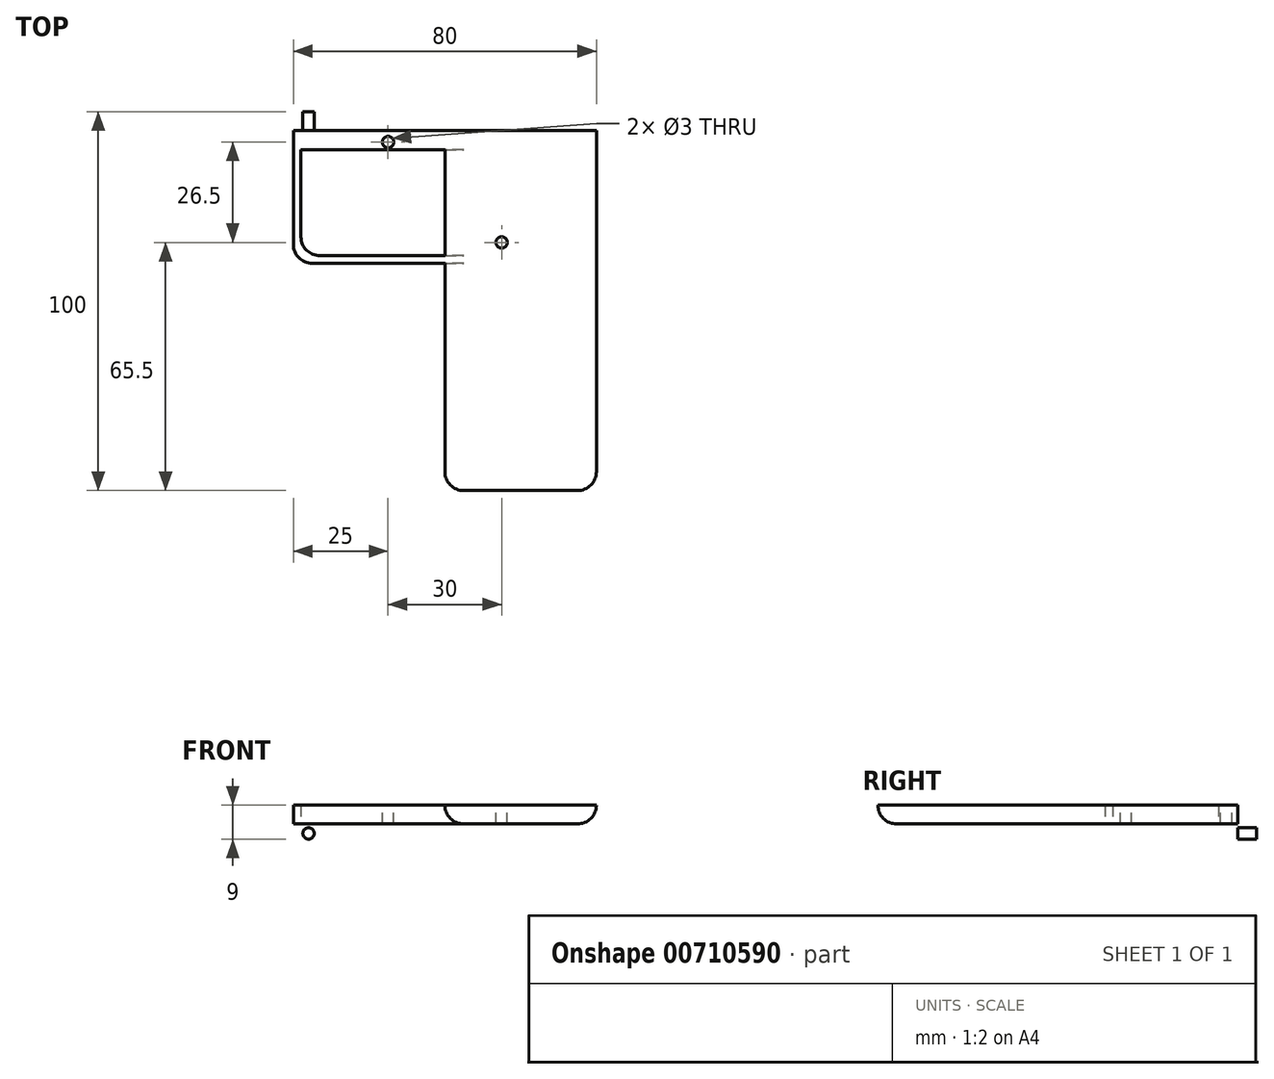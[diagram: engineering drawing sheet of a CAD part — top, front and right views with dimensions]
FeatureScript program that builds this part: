
annotation { "Feature Type Name" : "Feature", "Feature Type Description" : "" }
export const myFeature = defineFeature(function(context is Context, id is Id, definition is map)
    precondition{}
    {
        {
            var Q0;
            Q0=qCreatedBy(makeId("Top.planeOp"),FACE);
            var sketch = newSketch(context, id + "F0", { "sketchPlane" : qUnion([Q0])});
            skLineSegment(sketch, "E0.bottom", {"start": v(20, 50) * mm, "end": v(-20, 50) * mm});
            skLineSegment(sketch, "E0.top", {"start": v(20, -50) * mm, "end": v(-20, -50) * mm});
            skLineSegment(sketch, "E0.left", {"start": v(20, 50) * mm, "end": v(20, -50) * mm});
            skLineSegment(sketch, "E0.right", {"start": v(-20, 50) * mm, "end": v(-20, -50) * mm});
            skPoint(sketch, "E0.middle", {"position": v(0, 0) * mm});
            skLineSegment(sketch, "E1.bottom", {"start": v(-20, 50) * mm, "end": v(-60, 50) * mm});
            skLineSegment(sketch, "E1.top", {"start": v(-20, 10) * mm, "end": v(-60, 10) * mm});
            skLineSegment(sketch, "E1.left", {"start": v(-20, 50) * mm, "end": v(-20, 10) * mm});
            skLineSegment(sketch, "E1.right", {"start": v(-60, 50) * mm, "end": v(-60, 10) * mm});
            skLineSegment(sketch, "E2", {"start": v(-60, 50) * mm, "end": v(-58, 50) * mm});
            skLineSegment(sketch, "E3", {"start": v(-58, 50) * mm, "end": v(-58, 40) * mm});
            skLineSegment(sketch, "E4", {"start": v(-20, 10) * mm, "end": v(-20, 12) * mm});
            skLineSegment(sketch, "E5.bottom", {"start": v(-20, 12) * mm, "end": v(-58, 12) * mm});
            skLineSegment(sketch, "E5.top", {"start": v(-20, 40) * mm, "end": v(-58, 40) * mm});
            skLineSegment(sketch, "E5.left", {"start": v(-20, 12) * mm, "end": v(-20, 40) * mm});
            skLineSegment(sketch, "E5.right", {"start": v(-58, 12) * mm, "end": v(-58, 40) * mm});
            skSolve(sketch);
        }
        {
            var Q0;
            Q0=makeQuery(id+"F0.imprint","IMPRINT",FACE,{"disambiguationData":[TD([[makeQuery(id+"F0.imprint","IMPRINT",EDGE,{"derivedFrom":sQuery(id+"F0.wireOp",EDGE,"E0.bottom")}),1.0]])]});
            var Q1;
            Q1=makeQuery(id+"F0.imprint","IMPRINT",FACE,{"disambiguationData":[TD([[makeQuery(id+"F0.imprint","IMPRINT",EDGE,{"derivedFrom":sQuery(id+"F0.wireOp",EDGE,"E1.bottom")}),1.0]])]});
            var Q2;
            Q2=makeQuery(id+"F0.imprint","IMPRINT",FACE,{"disambiguationData":[TD([[makeQuery(id+"F0.imprint","IMPRINT",EDGE,{"derivedFrom":sQuery(id+"F0.wireOp",EDGE,"E1.top")}),-1.0]])]});
            extrude(context, id + "F1", {"entities" : qUnion([Q0, Q1, Q2]), "depth" : 5 * mm, "offsetDistance" : 25 * mm});
        }
        {
            var Q0;
            Q0=makeQuery(id+"F1.opExtrude","CAP_FACE",FACE,{"disambiguationData":[OSD([sQuery(id+"F0.wireOp",EDGE,"E0.bottom"),sQuery(id+"F0.wireOp",EDGE,"E0.top"),sQuery(id+"F0.wireOp",EDGE,"E0.left"),sQuery(id+"F0.wireOp",EDGE,"E0.right"),sQuery(id+"F0.wireOp",EDGE,"E1.bottom"),sQuery(id+"F0.wireOp",EDGE,"E1.top"),sQuery(id+"F0.wireOp",EDGE,"E1.right"),sQuery(id+"F0.wireOp",EDGE,"E2"),sQuery(id+"F0.wireOp",EDGE,"E5.bottom"),sQuery(id+"F0.wireOp",EDGE,"E5.top"),sQuery(id+"F0.wireOp",EDGE,"E5.left"),sQuery(id+"F0.wireOp",EDGE,"E5.right")])],"isStart":false});
            var sketch = newSketch(context, id + "F2", { "sketchPlane" : qUnion([Q0])});
            skLineSegment(sketch, "E6", {"start": v(-20, 40) * mm, "end": v(-35, 40) * mm, "construction": true});
            skLineSegment(sketch, "E7", {"start": v(-35, 40) * mm, "end": v(-35, 42) * mm, "construction": true});
            skCircle(sketch, "E8", {"center": v(-35, 42) * mm, "radius": 1.5 * mm});
            skLineSegment(sketch, "E9", {"start": v(-35, 42) * mm, "end": v(-35, 18.5) * mm, "construction": true});
            skLineSegment(sketch, "E10", {"start": v(-35, 18.5) * mm, "end": v(-5, 18.5) * mm, "construction": true});
            skLineSegment(sketch, "E11", {"start": v(-5, 18.5) * mm, "end": v(-5, 15.5) * mm, "construction": true});
            skCircle(sketch, "E12", {"center": v(-5, 15.5) * mm, "radius": 1.5 * mm});
            skLineSegment(sketch, "E13", {"start": v(20, 50) * mm, "end": v(20, 45) * mm});
            skLineSegment(sketch, "E14", {"start": v(20, 45) * mm, "end": v(15, 45) * mm});
            skLineSegment(sketch, "E15", {"start": v(15, 45) * mm, "end": v(15, 50) * mm});
            skSolve(sketch);
        }
        {
            var Q0;
            Q0=makeQuery(id+"F2.imprint","IMPRINT",FACE,{"disambiguationData":[TD([[makeQuery(id+"F2.imprint","IMPRINT",EDGE,{"derivedFrom":sQuery(id+"F2.wireOp",EDGE,"E8")}),1.0]])]});
            var Q1;
            Q1=makeQuery(id+"F2.imprint","IMPRINT",FACE,{"disambiguationData":[TD([[makeQuery(id+"F2.imprint","IMPRINT",EDGE,{"derivedFrom":sQuery(id+"F2.wireOp",EDGE,"E12")}),1.0]])]});
            var Q2;
            Q2=makeQuery(id+"F2.imprint","IMPRINT",FACE,{"disambiguationData":[TD([[makeQuery(id+"F2.imprint","IMPRINT",EDGE,{"derivedFrom":sQuery(id+"F2.wireOp",EDGE,"vCmjWVmu-7WJX-9hG4-9sAc-bVtIOR9l7AIR")}),1.0]])]});
            extrude(context, id + "F3", {"entities" : qUnion([Q0, Q1, Q2]), "operationType" : NewBodyOperationType.REMOVE, "oppositeDirection" : true, "depth" : 5 * mm, "offsetDistance" : 25 * mm});
        }
        {
            var Q0;
            Q0=makeQuery(id+"F1.opExtrude","CAP_FACE",FACE,{"disambiguationData":[OSD([sQuery(id+"F0.wireOp",EDGE,"E0.bottom"),sQuery(id+"F0.wireOp",EDGE,"E0.top"),sQuery(id+"F0.wireOp",EDGE,"E0.left"),sQuery(id+"F0.wireOp",EDGE,"E0.right"),sQuery(id+"F0.wireOp",EDGE,"E1.bottom"),sQuery(id+"F0.wireOp",EDGE,"E1.top"),sQuery(id+"F0.wireOp",EDGE,"E1.right"),sQuery(id+"F0.wireOp",EDGE,"E2"),sQuery(id+"F0.wireOp",EDGE,"E5.bottom"),sQuery(id+"F0.wireOp",EDGE,"E5.top"),sQuery(id+"F0.wireOp",EDGE,"E5.left"),sQuery(id+"F0.wireOp",EDGE,"E5.right")])],"isStart":true});
            var sketch = newSketch(context, id + "F4", { "sketchPlane" : qUnion([Q0])});
            skLineSegment(sketch, "E16", {"start": v(20, -50) * mm, "end": v(12, -50) * mm});
            skLineSegment(sketch, "E17", {"start": v(12, -50) * mm, "end": v(12, -45) * mm});
            skLineSegment(sketch, "E18", {"start": v(12, -45) * mm, "end": v(20, -45) * mm});
            skLineSegment(sketch, "E19.MirrorCS", {"start": v(-52, -50) * mm, "end": v(-52, -45) * mm});
            skLineSegment(sketch, "E20.MirrorCS", {"start": v(-52, -45) * mm, "end": v(-60, -45) * mm});
            skSolve(sketch);
        }
        {
            var Q0;
            {var subQ0=sQuery(id+"F4.wireOp",EDGE,"E16");Q0=makeQuery(id+"F4.imprint","IMPRINT",FACE,{"disambiguationData":[TD([[makeQuery(id+"F4.imprint","IMPRINT",EDGE,{"derivedFrom":subQ0}),-1.0]])]});}
            var Q1;
            {var subQ0=sQuery(id+"F4.wireOp",EDGE,"E19.MirrorCS");Q1=makeQuery(id+"F4.imprint","IMPRINT",FACE,{"disambiguationData":[TD([[makeQuery(id+"F4.imprint","IMPRINT",EDGE,{"derivedFrom":subQ0}),1.0]])]});}
            extrude(context, id + "F5", {"entities" : qUnion([Q0, Q1]), "operationType" : NewBodyOperationType.ADD, "depth" : 5 * mm, "offsetDistance" : 25 * mm});
        }
        {
            var Q0;
            Q0=makeQuery(id+"F5.boolean.opBoolean","MERGE",FACE,{"derivedFrom":[makeQuery(id+"F1.opExtrude","SWEPT_FACE",FACE,{"disambiguationData":[OSD([sQuery(id+"F0.wireOp",EDGE,"E0.bottom"),sQuery(id+"F0.wireOp",EDGE,"E1.bottom"),sQuery(id+"F0.wireOp",EDGE,"E2")])]}),makeQuery(id+"F5.opExtrude","SWEPT_FACE",FACE,{"disambiguationData":[OSD([sQuery(id+"F4.wireOp",EDGE,"E16")])]})]});
            var sketch = newSketch(context, id + "F6", { "sketchPlane" : qUnion([Q0])});
            skLineSegment(sketch, "E21", {"start": v(-20, -5) * mm, "end": v(-20, -2.5) * mm});
            skLineSegment(sketch, "E22", {"start": v(-20, -2.5) * mm, "end": v(-16, -2.5) * mm});
            skCircle(sketch, "E23", {"center": v(-16, -2.5) * mm, "radius": 1.5 * mm});
            skLineSegment(sketch, "E24", {"start": v(20, 0) * mm, "end": v(20, 5) * mm, "construction": true});
            skCircle(sketch, "E25.MirrorC", {"center": v(56, -2.5) * mm, "radius": 1.5 * mm});
            skSolve(sketch);
        }
        {
            var Q0;
            Q0=makeQuery(id+"F6.imprint","IMPRINT",FACE,{"disambiguationData":[TD([[makeQuery(id+"F6.imprint","IMPRINT",EDGE,{"derivedFrom":sQuery(id+"F6.wireOp",EDGE,"E23")}),1.0]])]});
            var Q1;
            Q1=makeQuery(id+"F6.imprint","IMPRINT",FACE,{"disambiguationData":[TD([[makeQuery(id+"F6.imprint","IMPRINT",EDGE,{"derivedFrom":sQuery(id+"F6.wireOp",EDGE,"E25.MirrorC")}),-1.0]])]});
            extrude(context, id + "F7", {"entities" : qUnion([Q0, Q1]), "operationType" : NewBodyOperationType.REMOVE, "oppositeDirection" : true, "depth" : 5 * mm, "offsetDistance" : 25 * mm});
        }
        {
            var Q0;
            Q0=makeQuery(id+"F1.opExtrude","CAP_EDGE",EDGE,{"disambiguationData":[OSD([sQuery(id+"F0.wireOp",EDGE,"E0.left")])],"isStart":true});
            var Q1;
            Q1=makeQuery(id+"F1.opExtrude","CAP_EDGE",EDGE,{"disambiguationData":[OSD([sQuery(id+"F0.wireOp",EDGE,"E5.left")])],"isStart":true});
            var Q2;
            Q2=makeQuery(id+"F1.opExtrude","CAP_EDGE",EDGE,{"disambiguationData":[OSD([sQuery(id+"F0.wireOp",EDGE,"E0.right")])],"isStart":true});
            var Q3;
            Q3=makeQuery(id+"F1.opExtrude","SWEPT_EDGE",EDGE,{"disambiguationData":[OSD([sQuery(id+"F0.wireOp",EDGE,"E0.top"),sQuery(id+"F0.wireOp",EDGE,"E0.left")])]});
            var Q4;
            Q4=makeQuery(id+"F1.opExtrude","CAP_EDGE",EDGE,{"disambiguationData":[OSD([sQuery(id+"F0.wireOp",EDGE,"E0.top")])],"isStart":true});
            var Q5;
            Q5=makeQuery(id+"F1.opExtrude","SWEPT_EDGE",EDGE,{"disambiguationData":[OSD([sQuery(id+"F0.wireOp",EDGE,"E0.top"),sQuery(id+"F0.wireOp",EDGE,"E0.right")])]});
            var Q6;
            Q6=makeQuery(id+"F1.opExtrude","SWEPT_EDGE",EDGE,{"disambiguationData":[OSD([sQuery(id+"F0.wireOp",EDGE,"E5.bottom"),sQuery(id+"F0.wireOp",EDGE,"E5.right")])]});
            var Q7;
            Q7=makeQuery(id+"F1.opExtrude","SWEPT_EDGE",EDGE,{"disambiguationData":[OSD([sQuery(id+"F0.wireOp",EDGE,"E1.top"),sQuery(id+"F0.wireOp",EDGE,"E1.right")])]});
            fillet(context, id + "F8", {"entities" : qUnion([Q0, Q1, Q2, Q3, Q4, Q5, Q6, Q7]), "radius" : 5 * mm, "tangentPropagation" : true, "allowEdgeOverflow" : false});
        }
    });
